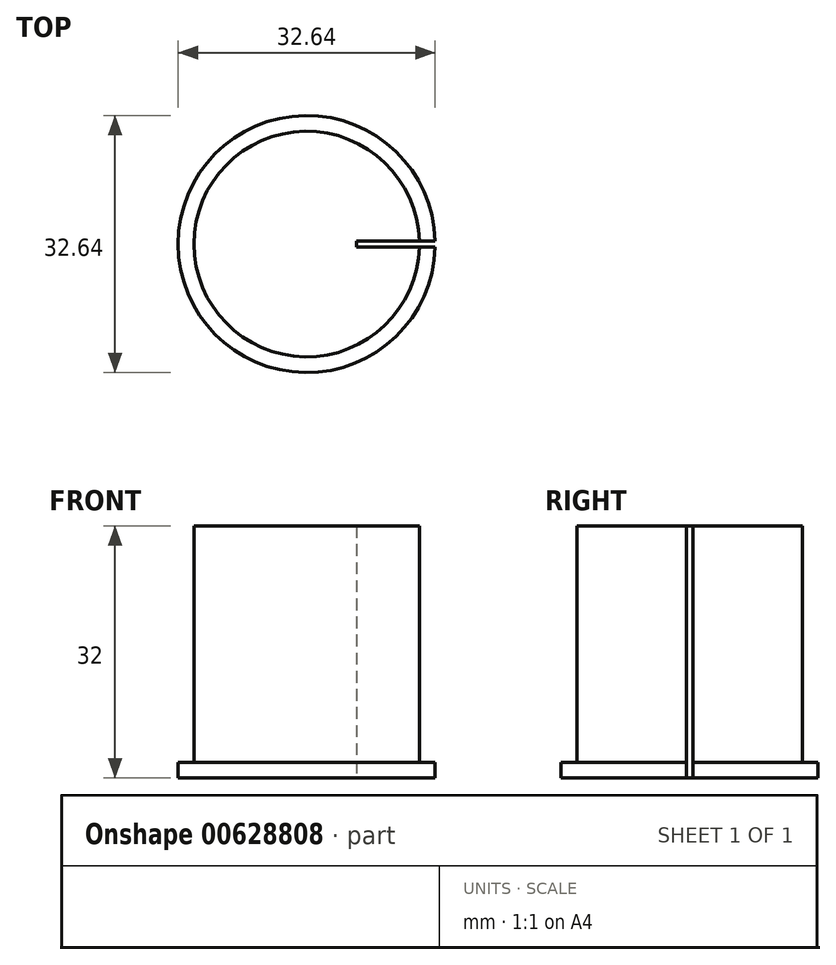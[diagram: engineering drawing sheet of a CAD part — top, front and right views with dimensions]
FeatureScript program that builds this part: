
annotation { "Feature Type Name" : "Feature", "Feature Type Description" : "" }
export const myFeature = defineFeature(function(context is Context, id is Id, definition is map)
    precondition{}
    {
        {
            var Q0;
            Q0=qCreatedBy(makeId("Top.planeOp"),FACE);
            var sketch = newSketch(context, id + "F0", { "sketchPlane" : qUnion([Q0])});
            skArc(sketch, "E0", {"start": v(14.32, 0.4) * mm, "mid": v(-14.32, 0) * mm, "end": v(14.32, -0.4) * mm});
            skArc(sketch, "E1", {"start": v(16.32, 0) * mm, "mid": v(-16.32, 0.2) * mm, "end": v(16.32, -0.4) * mm});
            skPoint(sketch, "E2", {"position": v(16.32, 0) * mm});
            skLineSegment(sketch, "E3", {"start": v(16.32, 0.4) * mm, "end": v(6.32, 0.4) * mm});
            skLineSegment(sketch, "E4", {"start": v(6.32, 0.4) * mm, "end": v(6.32, -0.4) * mm});
            skLineSegment(sketch, "E5", {"start": v(6.32, -0.4) * mm, "end": v(16.32, -0.4) * mm});
            skLineSegment(sketch, "E6", {"start": v(16.32, 0) * mm, "end": v(16.32, 0.4) * mm, "construction": true});
            skSolve(sketch);
        }
        {
            var Q0;
            Q0=makeQuery(id+"F0.imprint","IMPRINT",FACE,{"disambiguationData":[TD([[makeQuery(id+"F0.imprint","IMPRINT",EDGE,{"derivedFrom":sQuery(id+"F0.wireOp",EDGE,"E0")}),1.0]])]});
            extrude(context, id + "F1", {"entities" : qUnion([Q0]), "depth" : 30 * mm, "offsetDistance" : 25 * mm});
        }
        {
            var Q0;
            Q0=makeQuery(id+"F0.imprint","IMPRINT",FACE,{"disambiguationData":[TD([[makeQuery(id+"F0.imprint","IMPRINT",EDGE,{"derivedFrom":sQuery(id+"F0.wireOp",EDGE,"E0")}),-1.0]])]});
            var Q1;
            Q1=makeQuery(id+"F0.imprint","IMPRINT",FACE,{"disambiguationData":[TD([[makeQuery(id+"F0.imprint","IMPRINT",EDGE,{"derivedFrom":sQuery(id+"F0.wireOp",EDGE,"E0")}),1.0]])]});
            extrude(context, id + "F2", {"entities" : qUnion([Q0, Q1]), "operationType" : NewBodyOperationType.ADD, "oppositeDirection" : true, "depth" : 2 * mm, "offsetDistance" : 25 * mm});
        }
    });
